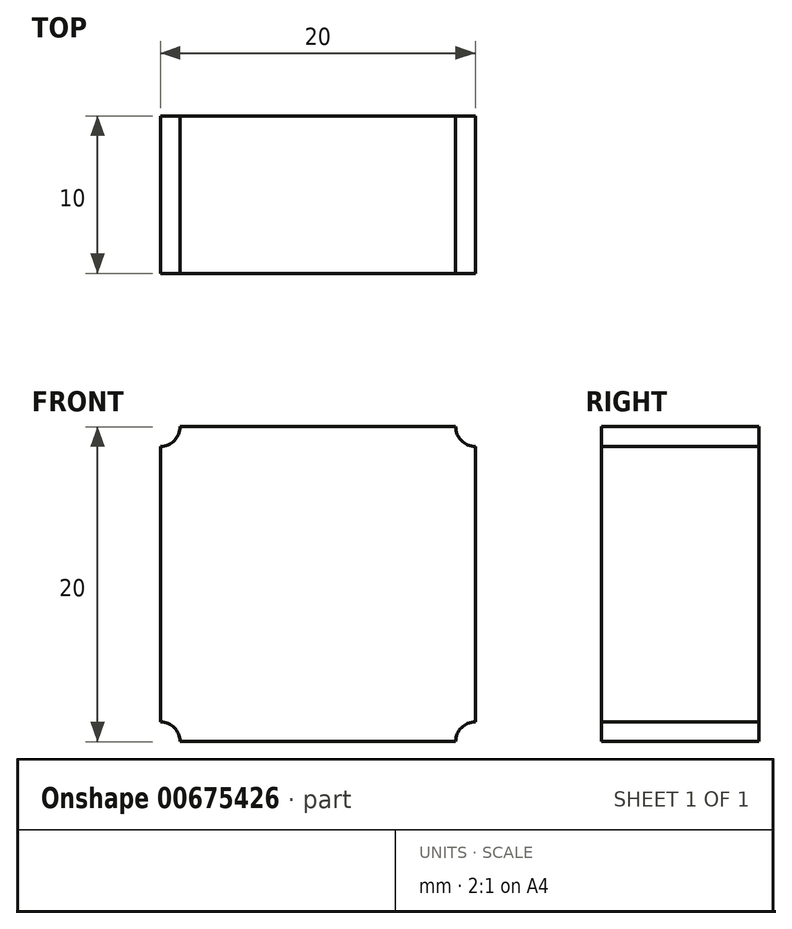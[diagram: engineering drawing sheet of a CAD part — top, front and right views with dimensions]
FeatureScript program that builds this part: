
annotation { "Feature Type Name" : "Feature", "Feature Type Description" : "" }
export const myFeature = defineFeature(function(context is Context, id is Id, definition is map)
    precondition{}
    {
        {
            var Q0;
            Q0=qCreatedBy(makeId("Front.planeOp"),FACE);
            var sketch = newSketch(context, id + "F0", { "sketchPlane" : qUnion([Q0])});
            skLineSegment(sketch, "E0", {"start": v(-34.16, 26.72) * mm, "end": v(-14.16, 26.72) * mm});
            skLineSegment(sketch, "E1", {"start": v(-14.16, 26.72) * mm, "end": v(-14.16, 6.72) * mm});
            skLineSegment(sketch, "E2", {"start": v(-14.16, 6.72) * mm, "end": v(-34.16, 6.72) * mm});
            skLineSegment(sketch, "E3", {"start": v(-34.16, 6.72) * mm, "end": v(-34.16, 26.72) * mm});
            skCircle(sketch, "E4", {"center": v(-34.16, 26.72) * mm, "radius": 1.25 * mm});
            skCircle(sketch, "E5", {"center": v(-14.16, 26.72) * mm, "radius": 1.25 * mm});
            skCircle(sketch, "E6", {"center": v(-34.16, 6.72) * mm, "radius": 1.25 * mm});
            skCircle(sketch, "E7", {"center": v(-14.16, 6.72) * mm, "radius": 1.25 * mm});
            skLineSegment(sketch, "E8", {"start": v(-34.16, 16.72) * mm, "end": v(-11.66, 16.72) * mm});
            skLineSegment(sketch, "E9", {"start": v(-11.66, 16.72) * mm, "end": v(-11.66, 29.22) * mm});
            skLineSegment(sketch, "E10", {"start": v(-11.66, 29.22) * mm, "end": v(-36.66, 29.22) * mm});
            skLineSegment(sketch, "E11", {"start": v(-36.66, 29.22) * mm, "end": v(-36.66, 4.22) * mm});
            skLineSegment(sketch, "E12", {"start": v(-36.66, 4.22) * mm, "end": v(-11.66, 4.22) * mm});
            skLineSegment(sketch, "E13", {"start": v(-11.66, 4.22) * mm, "end": v(-11.66, 16.72) * mm});
            skSolve(sketch);
        }
        {
            var Q0;
            {var subQ0=sQuery(id+"F0.wireOp",EDGE,"E8");var subQ5=sQuery(id+"F0.wireOp",EDGE,"E1");var subQ6=makeQuery(id+"F0.imprint","INTERSECT",VERTEX,{"derivedFrom":[subQ5,subQ0]});Q0=makeQuery(id+"F0.imprint","IMPRINT",FACE,{"disambiguationData":[TD([[makeQuery(id+"F0.imprint","IMPRINT",EDGE,{"disambiguationData":[TD([[subQ6,-1.0]])],"derivedFrom":subQ5}),-1.0]])]});}
            var Q1;
            {var subQ0=sQuery(id+"F0.wireOp",EDGE,"E4");var subQ1=sQuery(id+"F0.wireOp",EDGE,"E0");var subQ2=makeQuery(id+"F0.imprint","INTERSECT",VERTEX,{"derivedFrom":[subQ1,subQ0]});Q1=makeQuery(id+"F0.imprint","IMPRINT",FACE,{"disambiguationData":[TD([[makeQuery(id+"F0.imprint","IMPRINT",EDGE,{"disambiguationData":[TD([[subQ2,-1.0]])],"derivedFrom":subQ1}),-1.0]])]});}
            var Q2;
            Q2=makeQuery(id+"F0.imprint","IMPRINT",FACE,{"disambiguationData":[TD([[makeQuery(id+"F0.imprint","IMPRINT",EDGE,{"derivedFrom":sQuery(id+"F0.wireOp",EDGE,"E9")}),1.0]])]});
            extrude(context, id + "F1", {"entities" : qUnion([Q0, Q1, Q2]), "depth" : 10 * mm, "offsetDistance" : 25 * mm});
        }
    });
